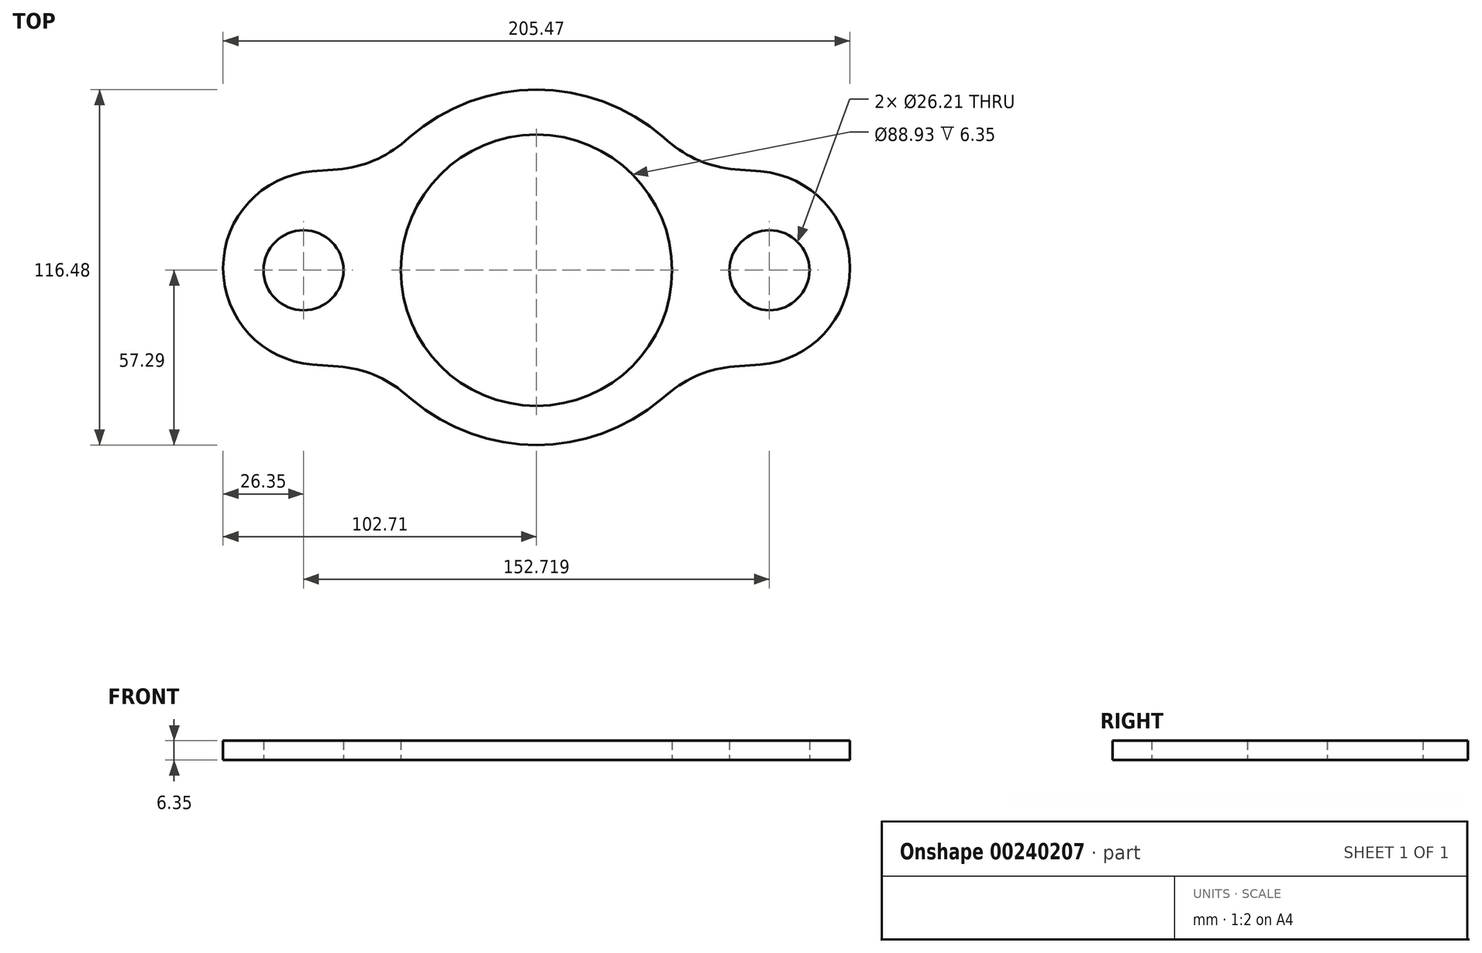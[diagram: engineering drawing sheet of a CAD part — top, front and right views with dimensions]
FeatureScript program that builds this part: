
annotation { "Feature Type Name" : "Feature", "Feature Type Description" : "" }
export const myFeature = defineFeature(function(context is Context, id is Id, definition is map)
    precondition{}
    {
        {
            var Q0;
            Q0=qCreatedBy(makeId("Top.planeOp"),FACE);
            var sketch = newSketch(context, id + "F0", { "sketchPlane" : qUnion([Q0])});
            skCircle(sketch, "E0", {"center": v(0, 0) * mm, "radius": 44.47 * mm});
            skLineSegment(sketch, "E1", {"start": v(0, 0) * mm, "end": v(-76.36, 0) * mm});
            skLineSegment(sketch, "E2", {"start": v(0, 0) * mm, "end": v(76.36, 0) * mm});
            skCircle(sketch, "E3", {"center": v(-76.36, 0) * mm, "radius": 13.1 * mm});
            skCircle(sketch, "E4", {"center": v(76.36, 0) * mm, "radius": 13.1 * mm});
            skLineSegment(sketch, "E5", {"start": v(-73.5, 32.4) * mm, "end": v(-65.11, 33.08) * mm});
            skLineSegment(sketch, "E6", {"start": v(-43.1, 42.36) * mm, "end": v(-41.78, 43.51) * mm});
            skLineSegment(sketch, "E7", {"start": v(41.78, 43.51) * mm, "end": v(43.09, 42.37) * mm});
            skLineSegment(sketch, "E8", {"start": v(65.12, 33.08) * mm, "end": v(73.54, 32.4) * mm});
            skLineSegment(sketch, "E9", {"start": v(73.42, -30.9) * mm, "end": v(64.86, -31.55) * mm});
            skLineSegment(sketch, "E10", {"start": v(43.15, -40.45) * mm, "end": v(41.01, -42.27) * mm});
            skLineSegment(sketch, "E11", {"start": v(-41.01, -42.27) * mm, "end": v(-43.16, -40.45) * mm});
            skLineSegment(sketch, "E12", {"start": v(-64.86, -31.55) * mm, "end": v(-73.38, -30.9) * mm});
            skPoint(sketch, "E13.visualSharp", {"position": v(-52.57, 34.08) * mm});
            skArc(sketch, "E13.filletArc", {"start": v(-65.11, 33.08) * mm, "mid": v(-53.35, 35.95) * mm, "end": v(-43.1, 42.36) * mm});
            skPoint(sketch, "E14.visualSharp", {"position": v(52.57, 34.08) * mm});
            skArc(sketch, "E14.filletArc", {"start": v(43.09, 42.37) * mm, "mid": v(53.35, 35.95) * mm, "end": v(65.12, 33.08) * mm});
            skPoint(sketch, "E15.visualSharp", {"position": v(52.57, -32.49) * mm});
            skArc(sketch, "E15.filletArc", {"start": v(64.86, -31.55) * mm, "mid": v(53.3, -34.3) * mm, "end": v(43.15, -40.45) * mm});
            skPoint(sketch, "E16.visualSharp", {"position": v(-52.57, -32.49) * mm});
            skArc(sketch, "E16.filletArc", {"start": v(-43.16, -40.45) * mm, "mid": v(-53.3, -34.29) * mm, "end": v(-64.86, -31.55) * mm});
            skPoint(sketch, "E17.visualSharp", {"position": v(0, -76.96) * mm});
            skArc(sketch, "E17.filletArc", {"start": v(-41.01, -42.27) * mm, "mid": v(0, -57.29) * mm, "end": v(41.01, -42.27) * mm});
            skPoint(sketch, "E18.visualSharp", {"position": v(0, 80) * mm});
            skArc(sketch, "E18.filletArc", {"start": v(41.78, 43.51) * mm, "mid": v(0, 59.19) * mm, "end": v(-41.78, 43.51) * mm});
            skPoint(sketch, "E19.visualSharp", {"position": v(478.68, 0) * mm});
            skArc(sketch, "E19.filletArc", {"start": v(73.42, -30.9) * mm, "mid": v(102.76, 0.7) * mm, "end": v(73.54, 32.4) * mm});
            skPoint(sketch, "E20.visualSharp", {"position": v(-477.7, 0) * mm});
            skArc(sketch, "E20.filletArc", {"start": v(-73.5, 32.4) * mm, "mid": v(-102.7, 0.7) * mm, "end": v(-73.38, -30.9) * mm});
            skSolve(sketch);
        }
        {
            var Q0;
            Q0=makeQuery(id+"F0.imprint","IMPRINT",FACE,{"disambiguationData":[TD([[makeQuery(id+"F0.imprint","IMPRINT",EDGE,{"derivedFrom":sQuery(id+"F0.wireOp",EDGE,"E3")}),-1.0]])]});
            extrude(context, id + "F1", {"entities" : qUnion([Q0]), "depth" : 6.35 * mm});
        }
    });
